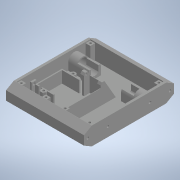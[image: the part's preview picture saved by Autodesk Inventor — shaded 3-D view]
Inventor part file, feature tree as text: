
AUTODESK INVENTOR PART (.ipt)
format: ipt  version: 2020 (Build 240168000, 168)  size: 615,936 bytes
history: native  units: in
note: dims shown in document units (in); Inventor stores cm internally (conversion verified against a paired STEP export)
features: extrude x18, sketch x17, projected_geometry x14, mirror x6, plane x1
ambient origin geometry x8: Origin, YZ Plane, XZ Plane, XY Plane, X Axis, Y Axis, Z Axis, Center Point
bodies: Solid1 (feature_tree)
feature tree (56):
  extrude  "Extrusion1"  Depth=5.9055in
  extrude  "Extrusion2"  TaperAngle=0.0deg  [1 undecoded]
  extrude  "Extrusion3"  Depth=1.063in
  extrude  "Extrusion4"  Depth=0.315in
  extrude  "Extrusion5"  TaperAngle=0.0deg  [1 undecoded]
  extrude  "Extrusion6"  Depth=0.5906in
  mirror  "Mirror1"
  extrude  "Extrusion7"  Depth=0.0787in
  mirror  "Mirror2"
  extrude  "Extrusion8"  Depth=0.6102in
  mirror  "Mirror3"
  plane  "Work Plane1"
  extrude  "Extrusion9"  Depth=0.7874in TaperAngle=0.0deg
  mirror  "Mirror4"
  extrude  "Extrusion10"  Depth=0.1654in TaperAngle=0.0deg
  extrude  "Extrusion11"  Depth=0.1575in
  extrude  "Extrusion12"  TaperAngle=0.0deg  [1 undecoded]
  extrude  "Extrusion13"  Depth=0.2756in
  extrude  "Extrusion14"  Depth=0.4331in
  extrude  "Extrusion17"  Depth=2.7559in
  extrude  "Extrusion18"  Depth=0.061in
  mirror  "Mirror6"
  extrude  "Extrusion19"  TaperAngle=0.0deg  [1 undecoded]
  mirror  "Mirror7"
  extrude  "Extrusion20"  TaperAngle=60.0deg  [1 undecoded]
  sketch  "Sketch1"  dims[d0=1.1811in d1=5.9055in]
  sketch  "Sketch2"  dims[d2=5.1181in d3=0.0in]
  projected_geometry  "Projected Loop1"
  sketch  "Sketch3"  dims[d4=0.1575in d5=1.063in]
  projected_geometry  "Projected Loop2"
  projected_geometry  "Projected Loop3"
  sketch  "Sketch4"  dims[d6=0.0in d8=0.315in]
  projected_geometry  "Projected Loop4"
  sketch  "Sketch6"  dims[d10=0.993in d11=0.0in]
  sketch  "Sketch7"  dims[d12=0.6496in d13=0.5906in]
  sketch  "Sketch9"  dims[d14=1.5748in d15=0.0787in]
  sketch  "Sketch10"  dims[d16=0.5512in d17=0.0in d18=0.6102in]
  sketch  "Sketch12"  dims[d19=0.4803in d20=0.7874in d21=0.0in]
  projected_geometry  "Projected Loop6"
  projected_geometry  "Projected Loop7"
  projected_geometry  "Projected Loop8"
  sketch  "Sketch13"  dims[d22=0.1654in d23=6.063in d24=0.0in]
  sketch  "Sketch14"  dims[d25=0.5114in d26=0.1575in]
  sketch  "Sketch15"  dims[d27=1.5748in d28=0.0in d29=0.0in]
  projected_geometry  "Projected Loop15"
  sketch  "Sketch16"  dims[d30=0.1575in d31=0.2756in]
  projected_geometry  "Projected Loop19"
  projected_geometry  "Projected Loop20"
  projected_geometry  "Projected Loop21"
  projected_geometry  "Projected Loop22"
  projected_geometry  "Projected Loop23"
  projected_geometry  "Projected Loop24"
  sketch  "Sketch20"  dims[d32=0.0in d33=0.4331in]
  sketch  "Sketch21"  dims[d34=0.122in d38=2.7559in]
  sketch  "Sketch22"  dims[d40=0.061in d41=0.0909in]
  sketch  "Sketch23"  dims[d42=0.2362in d43=0.0in d44=60.0deg d45=0.0787in d46=0.315in d48=0.993in d49=0.0in d53=0.2756in d54=0.0in d55=0.4724in d56=1.2008in d57=1.6142in d58=1.5945in d59=0.0787in d60=0.0787in d62=0.315in d63=0.7677in d64=0.0in d66=0.1476in d67=0.2756in d68=0.0in d69=0.7874in d70=0.2953in d71=0.1181in d72=0.0in d89=0.0157in d90=0.0157in d91=0.1476in d92=0.1476in d96=0.315in d97=0.1575in d98=0.1181in d99=0.0in d102=0.1772in d104=0.3346in d105=135.0deg d106=0.2362in d107=0.0in d108=0.0394in d109=0.0in d110=0.0315in d111=0.0394in d112=0.0in d114=0.0315in d115=0.5787in]
note: 5 required parameter values undecoded (feature->parameter linkage not recoverable at this tier; creation-order binding heuristic only, values carry confidence <= 0.55)
